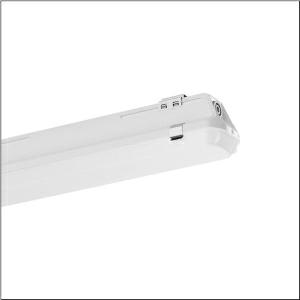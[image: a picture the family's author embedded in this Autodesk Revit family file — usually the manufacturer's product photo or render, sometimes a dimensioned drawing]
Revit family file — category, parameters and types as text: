
# Revit family: monsun_r__21_parking_51fg20dp440b_2f1b
name_source: partatom
category: Lighting Fixtures
units: mm (PartAtom-declared; Revit-internal decimal feet)

## family parameters
Cut with Voids When Loaded = No
Host = Face
Light Source = No
Part Type = Normal
Room Calculation Point = No
Round Connector Dimension = Use Diameter
Shared = No

## types (1)
- --- (1 x LED, 4810 lm, 34.4 W, 4000K)
    Apparent Load = 34 VA
    CIE Flux Codes = 45 75 93 94 100
    Color Rendering = 80
    Color Temperature = 4000K
    Default Elevation = 1800 mm
    Description = Monsun® 21 parking, damp-proof luminaire, chain hanger, primary optical cover: enclosure, of PC, light emission: direct distribution, primary light characteristic: symmetric, installation type: suspended mounting, surface-mounted, horizontal mounting, vertical mounting, LED, rated luminous flux: 4.810lm, luminous efficacy: 140lm/W, light colour: 840, colour temperature: 4000K, control gear: ECG DALI, with terminal, 5-pole, max. 2.5mm², mains connection: 220..240V, AC, 50/60Hz, rated input power: 34W, housing, of glass-fibre reinforced polyester, uncoated, bright grey, incl. chain hanger, length: 1.590mm, width: 90mm, height: 88mm, clip for enclosure, of stainless steel (V2A), ceiling mounting element, of stainless steel (V2A), chain hanger, of stainless steel (V2A), protection rating (complete): IP66, insulation class (complete): insulation class I (protective earthing), certification: CE, ENEC, VDE, UKCA, protection symbol: D, impact resistance: IK08, permissible operating ambient temperature: -25..+35°C, standard: EN 50419, EN 60598-2-1, corresponds to IFS (International Featured Standards) requirements for safety and quality in the food industry, for indoor or canopied outdoor use, no direct snow, no direct sun, no direct rain, contact your sales advisor before using the luminaires in applications with unclear chemical exposure, large temperature fluctuations or condensation-forming humidity, LABS conformity tested according to VDMA 24364:2018-05, packaging unit: 1 piece
    Height = 89 mm
    Lamp = 1 x LED
    Lamp Light Flux = 4810 lm
    Lamp Power = 34.4 W
    Lamp count = 1
    Length = 1590 mm
    Luminous efficacy = 140 lm/W
    Manufacturer = Siteco
    ModVariant = No
    Model = 51FG20DP440B
    Mounting Place = Ceiling
    Mounting Type = Surface mounted
    Number of Poles = 1
    OnlyDefault = Yes
    Power Factor = 1
    Product Name = Monsun® 21 parking
    Product group = damp-proof luminaire
    ProductGroupID = 300
    Protection Class = Protection class I
    Protection Degree = IP 66
    RLX_Detail_Level = 1
    RLX_Emergency_Light_Flux = 0 lm
    RLX_Emergency_Type = 0
    RLX_Emergency_Type_DB = No
    RlxData = <blob elided: 92301 chars, md5=699f705c>
    Socket = socket
    Standby Power = 0 W
    System Light Flux = 4810 lm
    System Power = 34 W
    Type Comments = factory setting: luminous flux: 100 % | dim-lin: 254 | 228 mA
    Type Image = l_1319656.jpg
    URL = http://relux.com
    VarID = @adj_171041
    Voltage = 0 V
    Weight = 0.00 kg
    Width = 90 mm

## geometry (parser evidence)
native form markers: Blend x4, Sweep x11
no freeform markers — native parametric forms only
